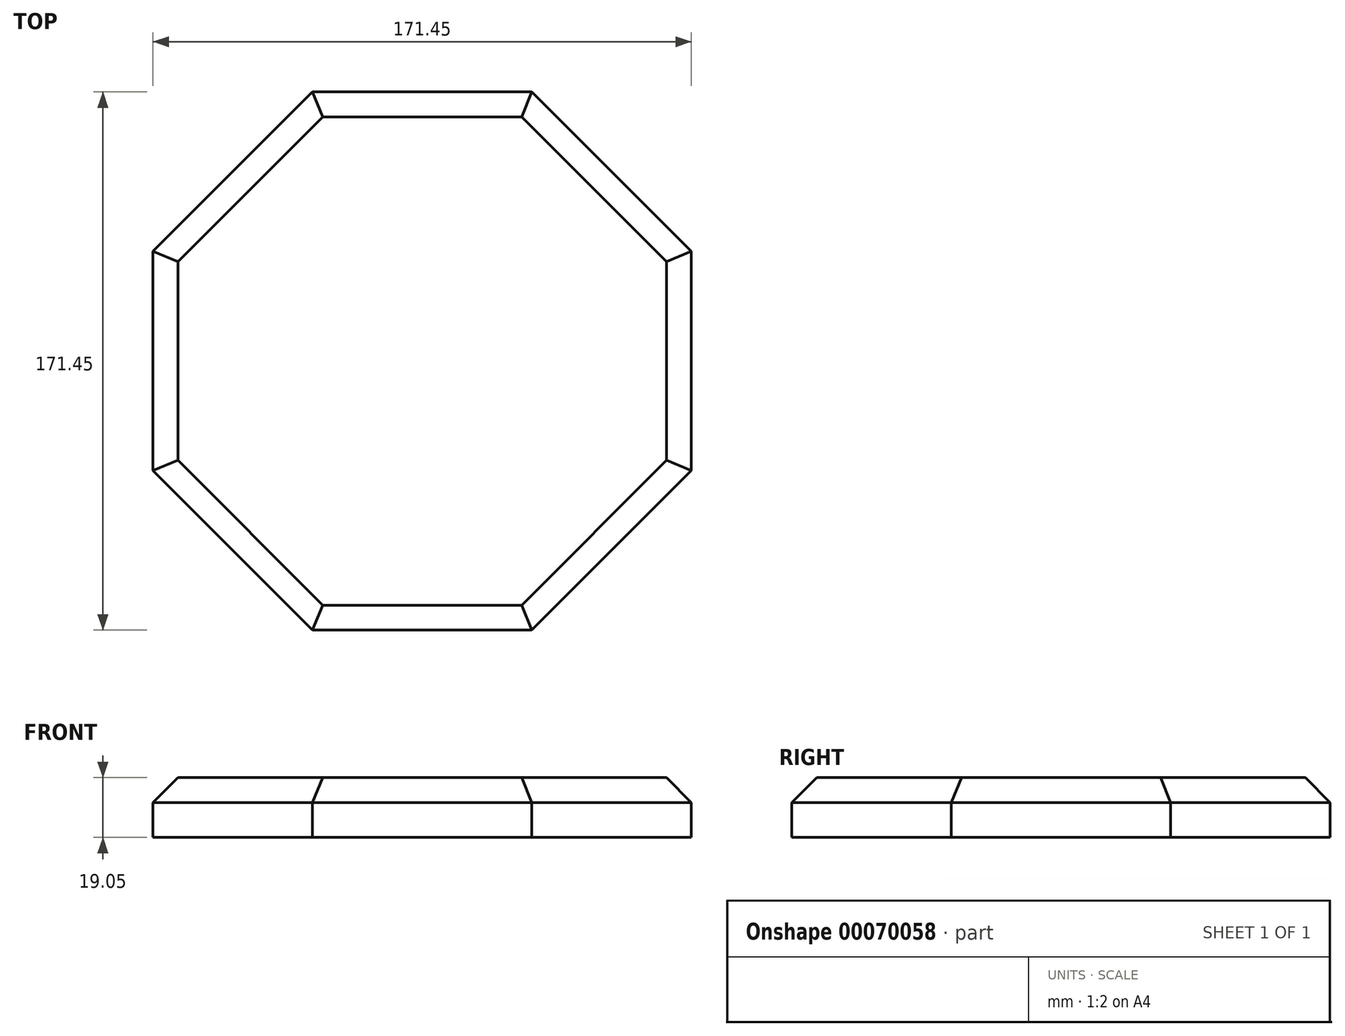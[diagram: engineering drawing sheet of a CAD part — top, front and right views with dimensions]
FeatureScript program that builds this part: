
annotation { "Feature Type Name" : "Feature", "Feature Type Description" : "" }
export const myFeature = defineFeature(function(context is Context, id is Id, definition is map)
    precondition{}
    {
        {
            var Q0;
            Q0=qCreatedBy(makeId("Top.planeOp"),FACE);
            var sketch = newSketch(context, id + "F0", { "sketchPlane" : qUnion([Q0])});
            skLineSegment(sketch, "E0.bottom", {"start": v(-85.73, 85.73) * mm, "end": v(85.73, 85.73) * mm});
            skLineSegment(sketch, "E0.top", {"start": v(-85.73, -85.73) * mm, "end": v(85.73, -85.73) * mm});
            skLineSegment(sketch, "E0.left", {"start": v(-85.73, 85.73) * mm, "end": v(-85.73, -85.73) * mm});
            skLineSegment(sketch, "E0.right", {"start": v(85.73, 85.73) * mm, "end": v(85.73, -85.73) * mm});
            skSolve(sketch);
        }
        {
            var Q0;
            Q0=makeQuery(id+"F0.imprint","IMPRINT",FACE,{"disambiguationData":[TD([[makeQuery(id+"F0.imprint","IMPRINT",EDGE,{"derivedFrom":sQuery(id+"F0.wireOp",EDGE,"E0.bottom")}),-1.0]])]});
            extrude(context, id + "F1", {"entities" : qUnion([Q0]), "depth" : 19.05 * mm});
        }
        {
            var Q0;
            Q0=makeQuery(id+"F1.opExtrude","CAP_FACE",FACE,{"disambiguationData":[OSD([sQuery(id+"F0.wireOp",EDGE,"E0.bottom"),sQuery(id+"F0.wireOp",EDGE,"E0.top"),sQuery(id+"F0.wireOp",EDGE,"E0.left"),sQuery(id+"F0.wireOp",EDGE,"E0.right"),sQuery(id+"F0.wireOp",EDGE,"989e4ac2-cbae-46ec-ac43-b30b8cb76129"),sQuery(id+"F0.wireOp",EDGE,"f01b9872-5823-4ad4-8aaf-3aa102a647f4"),sQuery(id+"F0.wireOp",EDGE,"f254082f-be6d-486d-81c3-8d4d65e6b824"),sQuery(id+"F0.wireOp",EDGE,"21b5d828-52df-4a59-b6f1-21bcb8ec3c0c"),sQuery(id+"F0.wireOp",EDGE,"d4020edf-602f-45da-a7a3-b06696fa117d"),sQuery(id+"F0.wireOp",EDGE,"905035b1-59ca-4ffc-a016-3912243c06da"),sQuery(id+"F0.wireOp",EDGE,"2c110506-1446-466a-9127-3dc12a78b58e"),sQuery(id+"F0.wireOp",EDGE,"26ce887d-3531-4269-9341-2fdd4bb3d620"),sQuery(id+"F0.wireOp",EDGE,"475ccb10-8f8e-49a7-93a4-93c3f0626b4c.bottom"),sQuery(id+"F0.wireOp",EDGE,"475ccb10-8f8e-49a7-93a4-93c3f0626b4c.top"),sQuery(id+"F0.wireOp",EDGE,"475ccb10-8f8e-49a7-93a4-93c3f0626b4c.left"),sQuery(id+"F0.wireOp",EDGE,"475ccb10-8f8e-49a7-93a4-93c3f0626b4c.right"),sQuery(id+"F0.wireOp",EDGE,"8ed021d0-fdce-44df-976c-de6f7beabc6d"),sQuery(id+"F0.wireOp",EDGE,"05c30dd9-ea8d-42c8-9be9-557685326a9e"),sQuery(id+"F0.wireOp",EDGE,"c46a8fb0-1c3f-46cc-903a-dbb448825e2e"),sQuery(id+"F0.wireOp",EDGE,"583893c2-0e6e-4aff-a0bb-19d91ca0a52e"),sQuery(id+"F0.wireOp",EDGE,"14300feb-ca35-44da-9651-15a41913f3c9.0"),sQuery(id+"F0.wireOp",EDGE,"8128e34a-8f59-4c2e-8099-998957f98d7b.0"),sQuery(id+"F0.wireOp",EDGE,"95882136-e9e6-4eb0-a4c0-31bc3ca21f6b.0"),sQuery(id+"F0.wireOp",EDGE,"ec29514e-9971-47f8-95a7-5a5ba83320e9.0")])],"isStart":false});
            var sketch = newSketch(context, id + "F2", { "sketchPlane" : qUnion([Q0])});
            skLineSegment(sketch, "E1", {"start": v(7.95, -33.34) * mm, "end": v(7.95, -20.64) * mm});
            skLineSegment(sketch, "E2", {"start": v(-33.34, 7.94) * mm, "end": v(-20.64, 7.94) * mm});
            skLineSegment(sketch, "E3", {"start": v(-20.64, -7.94) * mm, "end": v(-33.34, -7.94) * mm});
            skLineSegment(sketch, "E4", {"start": v(33.34, -9.24) * mm, "end": v(20.64, -9.24) * mm});
            skLineSegment(sketch, "E5.trimOffspring", {"start": v(-7.72, 33.34) * mm, "end": v(-7.8, 20.64) * mm});
            skPoint(sketch, "E6.center.orphan", {"position": v(0, -1.3) * mm});
            skLineSegment(sketch, "E7", {"start": v(-33.34, -7.94) * mm, "end": v(-33.34, 7.94) * mm});
            skLineSegment(sketch, "E8", {"start": v(33.34, -9.24) * mm, "end": v(33.34, 7.94) * mm});
            skPoint(sketch, "E8.startSnap0", {"position": v(33.34, -9.24) * mm});
            skLineSegment(sketch, "E9", {"start": v(-8.18, -33.34) * mm, "end": v(7.95, -33.34) * mm});
            skPoint(sketch, "E10.orphan", {"position": v(0, 20.64) * mm});
            skPoint(sketch, "E11.orphan", {"position": v(33.34, -6.04) * mm});
            skPoint(sketch, "E12.orphan", {"position": v(20.64, 0) * mm});
            skPoint(sketch, "E13.orphan", {"position": v(0, -20.64) * mm});
            skLineSegment(sketch, "E14.trimOffspring", {"start": v(20.64, 20.64) * mm, "end": v(20.64, 20.75) * mm});
            skPoint(sketch, "E15.orphan", {"position": v(-20.64, 0) * mm});
            skLineSegment(sketch, "E16.trimOffspring", {"start": v(20.75, 20.64) * mm, "end": v(20.64, 20.75) * mm});
            skLineSegment(sketch, "E17", {"start": v(-20.64, -7.94) * mm, "end": v(-8.1, -20.64) * mm});
            skLineSegment(sketch, "E18", {"start": v(20.64, -9.24) * mm, "end": v(7.95, -20.64) * mm});
            skLineSegment(sketch, "E19", {"start": v(-7.8, 20.64) * mm, "end": v(-20.64, 7.94) * mm});
            skLineSegment(sketch, "E20", {"start": v(-7.72, 33.34) * mm, "end": v(7.95, 33.34) * mm});
            skLineSegment(sketch, "E21", {"start": v(20.64, 7.94) * mm, "end": v(7.95, 20.64) * mm});
            skLineSegment(sketch, "E22.trimOffspring", {"start": v(20.64, 20.64) * mm, "end": v(20.75, 20.64) * mm});
            skLineSegment(sketch, "E23.trimOffspring", {"start": v(20.64, 7.94) * mm, "end": v(33.34, 7.94) * mm});
            skLineSegment(sketch, "E24.trimOffspring", {"start": v(-8.1, -20.64) * mm, "end": v(-8.18, -33.34) * mm});
            skLineSegment(sketch, "E25.trimOffspring", {"start": v(7.95, 20.64) * mm, "end": v(7.95, 33.34) * mm});
            skLineSegment(sketch, "E26", {"start": v(20.64, -9.24) * mm, "end": v(20.64, 7.94) * mm});
            skLineSegment(sketch, "E27", {"start": v(-20.64, -7.94) * mm, "end": v(-20.64, 7.94) * mm});
            skLineSegment(sketch, "E28", {"start": v(-7.8, 20.64) * mm, "end": v(7.95, 20.64) * mm});
            skLineSegment(sketch, "E29", {"start": v(-8.1, -20.64) * mm, "end": v(7.95, -20.64) * mm});
            skSolve(sketch);
        }
        {
            var Q0;
            Q0=makeQuery(id+"F2.imprint","IMPRINT",FACE,{"disambiguationData":[TD([[makeQuery(id+"F2.imprint","IMPRINT",EDGE,{"derivedFrom":sQuery(id+"F2.wireOp",EDGE,"E17")}),1.0]])]});
            extrude(context, id + "F3", {"entities" : qUnion([Q0]), "depth" : 127 * mm});
        }
        {
            var Q0;
            Q0=makeQuery(id+"F2.imprint","IMPRINT",FACE,{"disambiguationData":[TD([[makeQuery(id+"F2.imprint","IMPRINT",EDGE,{"derivedFrom":sQuery(id+"F2.wireOp",EDGE,"E4")}),-1.0]])]});
            extrude(context, id + "F4", {"entities" : qUnion([Q0]), "depth" : 203.2 * mm});
        }
        {
            var Q0;
            Q0=makeQuery(id+"F4.opExtrude","CAP_EDGE",EDGE,{"disambiguationData":[OSD([sQuery(id+"F2.wireOp",EDGE,"E8")])],"isStart":false});
            chamfer(context, id + "F5", {"entities" : qUnion([Q0]), "width" : 5.08 * mm, "tangentPropagation" : true});
        }
        {
            var Q0;
            Q0=makeQuery(id+"F2.imprint","IMPRINT",FACE,{"disambiguationData":[TD([[makeQuery(id+"F2.imprint","IMPRINT",EDGE,{"derivedFrom":sQuery(id+"F2.wireOp",EDGE,"E1")}),1.0]])]});
            extrude(context, id + "F6", {"entities" : qUnion([Q0]), "depth" : 177.8 * mm});
        }
        {
            var Q0;
            Q0=makeQuery(id+"F6.opExtrude","CAP_EDGE",EDGE,{"disambiguationData":[OSD([sQuery(id+"F2.wireOp",EDGE,"E9")])],"isStart":false});
            chamfer(context, id + "F7", {"entities" : qUnion([Q0]), "width" : 5.08 * mm, "tangentPropagation" : true});
        }
        {
            var Q0;
            Q0=makeQuery(id+"F2.imprint","IMPRINT",FACE,{"disambiguationData":[TD([[makeQuery(id+"F2.imprint","IMPRINT",EDGE,{"derivedFrom":sQuery(id+"F2.wireOp",EDGE,"E5.trimOffspring")}),1.0]])]});
            extrude(context, id + "F8", {"entities" : qUnion([Q0]), "depth" : 177.8 * mm});
        }
        {
            var Q0;
            Q0=makeQuery(id+"F8.opExtrude","CAP_EDGE",EDGE,{"disambiguationData":[OSD([sQuery(id+"F2.wireOp",EDGE,"E20")])],"isStart":false});
            chamfer(context, id + "F9", {"entities" : qUnion([Q0]), "width" : 5.08 * mm, "tangentPropagation" : true});
        }
        {
            var Q0;
            Q0=makeQuery(id+"F2.imprint","IMPRINT",FACE,{"disambiguationData":[TD([[makeQuery(id+"F2.imprint","IMPRINT",EDGE,{"derivedFrom":sQuery(id+"F2.wireOp",EDGE,"E2")}),-1.0]])]});
            extrude(context, id + "F10", {"entities" : qUnion([Q0]), "depth" : 152.4 * mm});
        }
        {
            var Q0;
            Q0=makeQuery(id+"F10.opExtrude","CAP_EDGE",EDGE,{"disambiguationData":[OSD([sQuery(id+"F2.wireOp",EDGE,"E7")])],"isStart":false});
            chamfer(context, id + "F11", {"entities" : qUnion([Q0]), "width" : 5.08 * mm, "tangentPropagation" : true});
        }
        {
            var Q0;
            Q0=makeQuery(id+"F1.opExtrude","SWEPT_EDGE",EDGE,{"disambiguationData":[OSD([sQuery(id+"F0.wireOp",EDGE,"E0.bottom"),sQuery(id+"F0.wireOp",EDGE,"E0.right")])]});
            var Q1;
            Q1=makeQuery(id+"F1.opExtrude","SWEPT_EDGE",EDGE,{"disambiguationData":[OSD([sQuery(id+"F0.wireOp",EDGE,"E0.bottom"),sQuery(id+"F0.wireOp",EDGE,"E0.left")])]});
            var Q2;
            Q2=makeQuery(id+"F1.opExtrude","SWEPT_EDGE",EDGE,{"disambiguationData":[OSD([sQuery(id+"F0.wireOp",EDGE,"E0.top"),sQuery(id+"F0.wireOp",EDGE,"E0.right")])]});
            var Q3;
            Q3=makeQuery(id+"F1.opExtrude","SWEPT_EDGE",EDGE,{"disambiguationData":[OSD([sQuery(id+"F0.wireOp",EDGE,"E0.top"),sQuery(id+"F0.wireOp",EDGE,"E0.left")])]});
            chamfer(context, id + "F12", {"entities" : qUnion([Q0, Q1, Q2, Q3]), "width" : 50.8 * mm, "tangentPropagation" : true});
        }
        {
            var Q0;
            {var subQ0=sQuery(id+"F0.wireOp",EDGE,"E0.left");var subQ1=sQuery(id+"F0.wireOp",EDGE,"E0.top");Q0=makeQuery(id+"F12.opChamfer","BLEND_EDGE",EDGE,{"blendedFrom":[makeQuery(id+"F1.opExtrude","SWEPT_EDGE",EDGE,{"disambiguationData":[OSD([subQ1,subQ0])]}),makeQuery(id+"F1.opExtrude","CAP_FACE",FACE,{"disambiguationData":[OSD([sQuery(id+"F0.wireOp",EDGE,"E0.bottom"),subQ1,subQ0,sQuery(id+"F0.wireOp",EDGE,"E0.right")])],"isStart":false})],"blendedInto":[makeQuery(id+"F1.opExtrude","CAP_FACE",FACE,{"disambiguationData":[OSD([sQuery(id+"F0.wireOp",EDGE,"E0.bottom"),subQ1,subQ0,sQuery(id+"F0.wireOp",EDGE,"E0.right")])],"isStart":false})]});}
            var Q1;
            Q1=makeQuery(id+"F1.opExtrude","CAP_EDGE",EDGE,{"disambiguationData":[OSD([sQuery(id+"F0.wireOp",EDGE,"E0.top")])],"isStart":false});
            var Q2;
            {var subQ0=sQuery(id+"F0.wireOp",EDGE,"E0.right");var subQ1=sQuery(id+"F0.wireOp",EDGE,"E0.top");Q2=makeQuery(id+"F12.opChamfer","BLEND_EDGE",EDGE,{"blendedFrom":[makeQuery(id+"F1.opExtrude","SWEPT_EDGE",EDGE,{"disambiguationData":[OSD([subQ1,subQ0])]}),makeQuery(id+"F1.opExtrude","CAP_FACE",FACE,{"disambiguationData":[OSD([sQuery(id+"F0.wireOp",EDGE,"E0.bottom"),subQ1,sQuery(id+"F0.wireOp",EDGE,"E0.left"),subQ0])],"isStart":false})],"blendedInto":[makeQuery(id+"F1.opExtrude","CAP_FACE",FACE,{"disambiguationData":[OSD([sQuery(id+"F0.wireOp",EDGE,"E0.bottom"),subQ1,sQuery(id+"F0.wireOp",EDGE,"E0.left"),subQ0])],"isStart":false})]});}
            var Q3;
            Q3=makeQuery(id+"F1.opExtrude","CAP_EDGE",EDGE,{"disambiguationData":[OSD([sQuery(id+"F0.wireOp",EDGE,"E0.right")])],"isStart":false});
            var Q4;
            {var subQ0=sQuery(id+"F0.wireOp",EDGE,"E0.right");var subQ1=sQuery(id+"F0.wireOp",EDGE,"E0.bottom");Q4=makeQuery(id+"F12.opChamfer","BLEND_EDGE",EDGE,{"blendedFrom":[makeQuery(id+"F1.opExtrude","SWEPT_EDGE",EDGE,{"disambiguationData":[OSD([subQ1,subQ0])]}),makeQuery(id+"F1.opExtrude","CAP_FACE",FACE,{"disambiguationData":[OSD([subQ1,sQuery(id+"F0.wireOp",EDGE,"E0.top"),sQuery(id+"F0.wireOp",EDGE,"E0.left"),subQ0])],"isStart":false})],"blendedInto":[makeQuery(id+"F1.opExtrude","CAP_FACE",FACE,{"disambiguationData":[OSD([subQ1,sQuery(id+"F0.wireOp",EDGE,"E0.top"),sQuery(id+"F0.wireOp",EDGE,"E0.left"),subQ0])],"isStart":false})]});}
            var Q5;
            Q5=makeQuery(id+"F1.opExtrude","CAP_EDGE",EDGE,{"disambiguationData":[OSD([sQuery(id+"F0.wireOp",EDGE,"E0.bottom")])],"isStart":false});
            var Q6;
            {var subQ0=sQuery(id+"F0.wireOp",EDGE,"E0.left");var subQ1=sQuery(id+"F0.wireOp",EDGE,"E0.bottom");Q6=makeQuery(id+"F12.opChamfer","BLEND_EDGE",EDGE,{"blendedFrom":[makeQuery(id+"F1.opExtrude","SWEPT_EDGE",EDGE,{"disambiguationData":[OSD([subQ1,subQ0])]}),makeQuery(id+"F1.opExtrude","CAP_FACE",FACE,{"disambiguationData":[OSD([subQ1,sQuery(id+"F0.wireOp",EDGE,"E0.top"),subQ0,sQuery(id+"F0.wireOp",EDGE,"E0.right")])],"isStart":false})],"blendedInto":[makeQuery(id+"F1.opExtrude","CAP_FACE",FACE,{"disambiguationData":[OSD([subQ1,sQuery(id+"F0.wireOp",EDGE,"E0.top"),subQ0,sQuery(id+"F0.wireOp",EDGE,"E0.right")])],"isStart":false})]});}
            var Q7;
            Q7=makeQuery(id+"F1.opExtrude","CAP_EDGE",EDGE,{"disambiguationData":[OSD([sQuery(id+"F0.wireOp",EDGE,"E0.left")])],"isStart":false});
            chamfer(context, id + "F13", {"entities" : qUnion([Q0, Q1, Q2, Q3, Q4, Q5, Q6, Q7]), "width" : 7.94 * mm, "tangentPropagation" : true});
        }
        {
            var Q0;
            Q0=makeQuery(id+"F3.opExtrude","CAP_FACE",FACE,{"disambiguationData":[OSD([sQuery(id+"F2.wireOp",EDGE,"E17"),sQuery(id+"F2.wireOp",EDGE,"E18"),sQuery(id+"F2.wireOp",EDGE,"E19"),sQuery(id+"F2.wireOp",EDGE,"E21"),sQuery(id+"F2.wireOp",EDGE,"E26"),sQuery(id+"F2.wireOp",EDGE,"E27"),sQuery(id+"F2.wireOp",EDGE,"E28"),sQuery(id+"F2.wireOp",EDGE,"E29")])],"isStart":false});
            var sketch = newSketch(context, id + "F14", { "sketchPlane" : qUnion([Q0])});
            skCircle(sketch, "E30", {"center": v(0, 0) * mm, "radius": 20.66 * mm});
            skSolve(sketch);
        }
        {
            var Q0;
            {var subQ0=sQuery(id+"F14.wireOp",EDGE,"E30");var subQ9=makeQuery(id+"F3.opExtrude","CAP_EDGE",EDGE,{"disambiguationData":[OSD([sQuery(id+"F2.wireOp",EDGE,"E21")])],"isStart":false});var subQ10=makeQuery(id+"F14.imprint","INTERSECT",VERTEX,{"disambiguationData":[OD(0.0)],"derivedFrom":[subQ9,subQ0]});Q0=makeQuery(id+"F14.imprint","IMPRINT",FACE,{"disambiguationData":[TD([[makeQuery(id+"F14.imprint","IMPRINT",EDGE,{"disambiguationData":[TD([[subQ10,1.0]])],"derivedFrom":subQ0}),1.0]])]});}
            var sketch = newSketch(context, id + "F15", { "sketchPlane" : qUnion([Q0])});
            skCircle(sketch, "E31", {"center": v(0, 0) * mm, "radius": 19.81 * mm});
            skSolve(sketch);
        }
        {
            var Q0;
            Q0 = qSketchRegion(id + "F15", true);
            extrude(context, id + "F16", {"entities" : qUnion([Q0]), "depth" : 355.6 * mm});
        }
        {
            var Q0;
            Q0=makeQuery(id+"F16.opExtrude","CAP_EDGE",EDGE,{"disambiguationData":[OSD([sQuery(id+"F15.wireOp",EDGE,"E31")])],"isStart":false});
            chamfer(context, id + "F17", {"entities" : qUnion([Q0]), "width" : 5.08 * mm, "tangentPropagation" : true});
        }
        {
            var Q0;
            {var subQ0=sQuery(id+"F14.wireOp",EDGE,"E30");var subQ9=makeQuery(id+"F3.opExtrude","CAP_EDGE",EDGE,{"disambiguationData":[OSD([sQuery(id+"F2.wireOp",EDGE,"E21")])],"isStart":false});var subQ10=makeQuery(id+"F14.imprint","INTERSECT",VERTEX,{"disambiguationData":[OD(0.0)],"derivedFrom":[subQ9,subQ0]});Q0=makeQuery(id+"F14.imprint","IMPRINT",FACE,{"disambiguationData":[TD([[makeQuery(id+"F14.imprint","IMPRINT",EDGE,{"disambiguationData":[TD([[subQ10,1.0]])],"derivedFrom":subQ0}),1.0]])]});}
            extrude(context, id + "F18", {"entities" : qUnion([Q0]), "depth" : 25.4 * mm});
        }
        {
            var Q0;
            Q0=makeQuery(id+"F16.opExtrude","SWEPT_BODY",BODY,{"disambiguationData":[OSD([sQuery(id+"F15.wireOp",EDGE,"E31")])]});
            deleteBodies(context, id + "F19", {"entities" : qUnion([Q0])});
        }
        {
            var Q0;
            Q0=makeQuery(id+"F4.opExtrude","SWEPT_BODY",BODY,{"disambiguationData":[OSD([sQuery(id+"F2.wireOp",EDGE,"E4"),sQuery(id+"F2.wireOp",EDGE,"E8"),sQuery(id+"F2.wireOp",EDGE,"E23.trimOffspring"),sQuery(id+"F2.wireOp",EDGE,"E26")])]});
            deleteBodies(context, id + "F20", {"entities" : qUnion([Q0])});
        }
        {
            var Q0;
            Q0=makeQuery(id+"F3.opExtrude","SWEPT_BODY",BODY,{"disambiguationData":[OSD([sQuery(id+"F2.wireOp",EDGE,"E17"),sQuery(id+"F2.wireOp",EDGE,"E18"),sQuery(id+"F2.wireOp",EDGE,"E19"),sQuery(id+"F2.wireOp",EDGE,"E21"),sQuery(id+"F2.wireOp",EDGE,"E26"),sQuery(id+"F2.wireOp",EDGE,"E27"),sQuery(id+"F2.wireOp",EDGE,"E28"),sQuery(id+"F2.wireOp",EDGE,"E29")])]});
            deleteBodies(context, id + "F21", {"entities" : qUnion([Q0])});
        }
        {
            var Q0;
            Q0=makeQuery(id+"F18.opExtrude","SWEPT_BODY",BODY,{"disambiguationData":[OSD([sQuery(id+"F2.wireOp",EDGE,"E17"),sQuery(id+"F2.wireOp",EDGE,"E19"),sQuery(id+"F2.wireOp",EDGE,"E21"),sQuery(id+"F2.wireOp",EDGE,"E26"),sQuery(id+"F2.wireOp",EDGE,"E27"),sQuery(id+"F2.wireOp",EDGE,"E28"),sQuery(id+"F2.wireOp",EDGE,"E29"),sQuery(id+"F14.wireOp",EDGE,"E30")])]});
            deleteBodies(context, id + "F22", {"entities" : qUnion([Q0])});
        }
        {
            var Q0;
            Q0=makeQuery(id+"F8.opExtrude","SWEPT_BODY",BODY,{"disambiguationData":[OSD([sQuery(id+"F2.wireOp",EDGE,"E5.trimOffspring"),sQuery(id+"F2.wireOp",EDGE,"E20"),sQuery(id+"F2.wireOp",EDGE,"E25.trimOffspring"),sQuery(id+"F2.wireOp",EDGE,"E28")])]});
            deleteBodies(context, id + "F23", {"entities" : qUnion([Q0])});
        }
        {
            var Q0;
            Q0=makeQuery(id+"F6.opExtrude","SWEPT_BODY",BODY,{"disambiguationData":[OSD([sQuery(id+"F2.wireOp",EDGE,"E1"),sQuery(id+"F2.wireOp",EDGE,"E9"),sQuery(id+"F2.wireOp",EDGE,"E24.trimOffspring"),sQuery(id+"F2.wireOp",EDGE,"E29")])]});
            deleteBodies(context, id + "F24", {"entities" : qUnion([Q0])});
        }
        {
            var Q0;
            Q0=makeQuery(id+"F10.opExtrude","SWEPT_BODY",BODY,{"disambiguationData":[OSD([sQuery(id+"F2.wireOp",EDGE,"E2"),sQuery(id+"F2.wireOp",EDGE,"E3"),sQuery(id+"F2.wireOp",EDGE,"E7"),sQuery(id+"F2.wireOp",EDGE,"E27")])]});
            deleteBodies(context, id + "F25", {"entities" : qUnion([Q0])});
        }
    });
